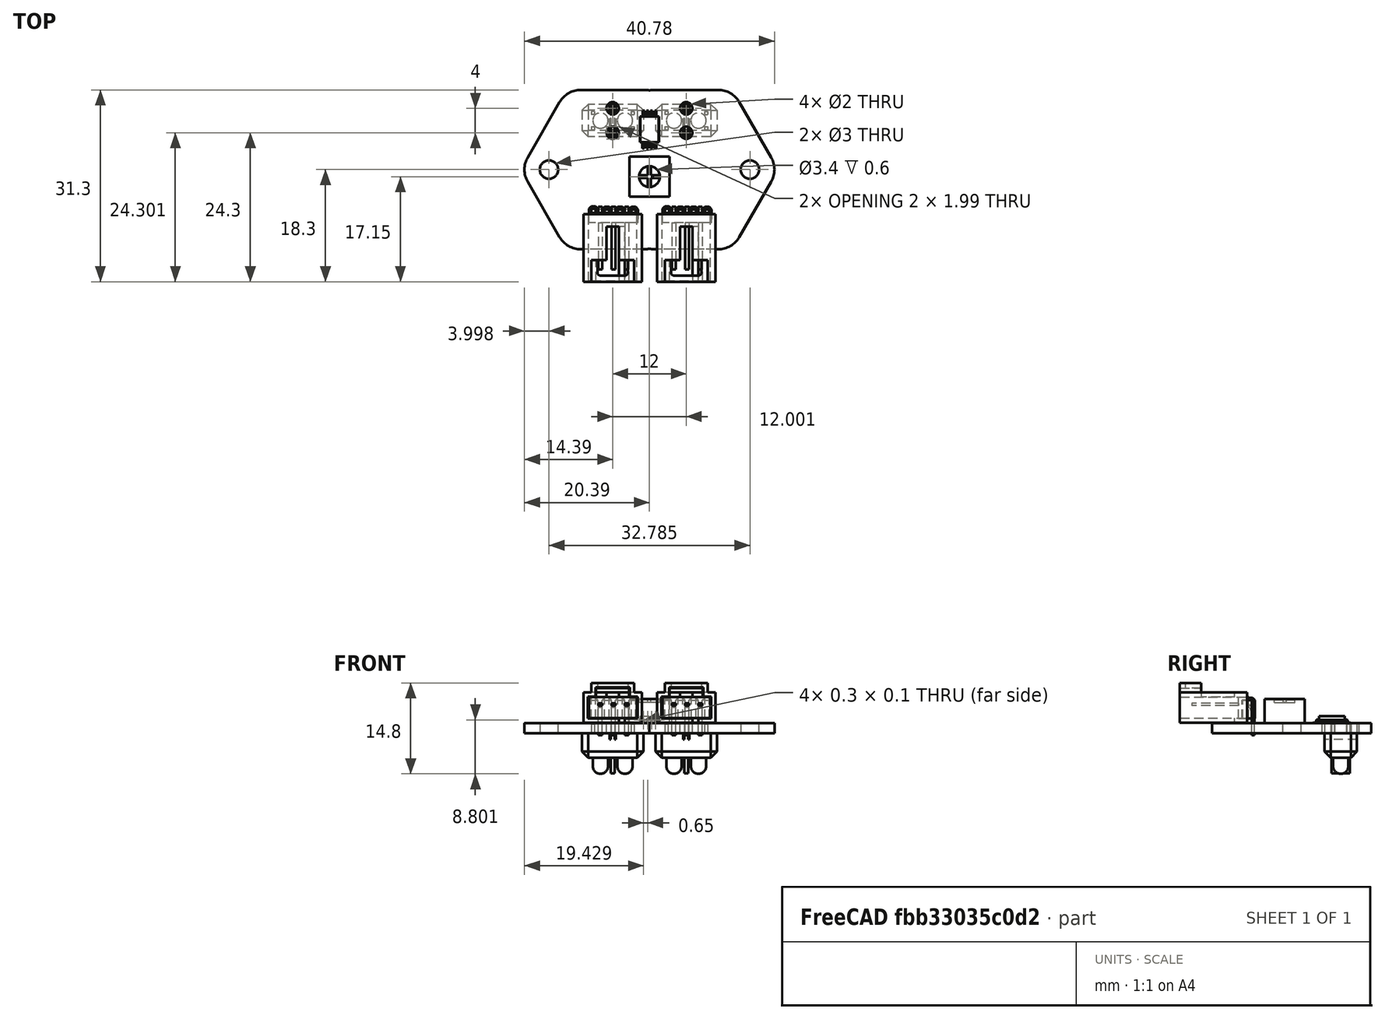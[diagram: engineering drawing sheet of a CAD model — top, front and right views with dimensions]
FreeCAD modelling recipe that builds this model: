
FCSTD DOCUMENT  (FreeCAD 0.14R3692 (Git))
Label: ZumIR_dos
License: CC-BY 3.0
LicenseURL: http://creativecommons.org/licenses/by/3.0/
objects: Part::MultiFuse×7, Part::Cut×6, Part::Cylinder×2, App::DocumentObjectGroup×2
note: 15 computed .brp shape members not serialized (recipe doc carries the construction recipe); baked Part::Feature solids carry a one-line shape summary decoded from their .brp

FEATURE [Part::Cut] Cut  label="Placa_ZumSingle"
FEATURE [Part::Cut] Cut001  label="Placa_ZumSingle001"
  Placement = pos=(12,0,0) rot=(0,0,1;0rad)
FEATURE [Part::MultiFuse] Fusion
  Shapes = -> [Cut,Cut001]
FEATURE [Part::Cylinder] Cylinder  label="Cilindro001"
  Angle = 360
  Height = 10
  Placement = pos=(0,6,-2) rot=(0,0,1;0rad)
  Radius = 1
FEATURE [Part::Cylinder] Cylinder001  label="Cilindro002"
  Angle = 360
  Height = 10
  Placement = pos=(12,6,-2) rot=(0,0,1;0rad)
  Radius = 1
FEATURE [Part::Cut] Cut002
  Base = -> Fusion
  Tool = -> Cylinder
FEATURE [Part::Cut] Cut003
  Base = -> Cut002
  Placement = pos=(-6,0,0) rot=(0,0,1;0rad)
  Tool = -> Cylinder001
FEATURE [Part::MultiFuse] Fusion001  label="Potenciometro001"
  Placement = pos=(0,-1.15,1.6) rot=(0,0,1;0rad)
  Shapes = -> [Cut002,Cut001]
FEATURE [Part::MultiFuse] Fusion002  label="Conectores"
  Placement = pos=(-6,0.7,0.7) rot=(0,0,1;1.5708rad)
FEATURE [Part::Cut] Cut004  label="AlojaConectores"
  Placement = pos=(-6,0.7,0.7) rot=(0,0,1;1.5708rad)
FEATURE [App::DocumentObjectGroup] Grupo  label="GR_Conector"
  Group = -> [Cut004,Fusion002]
FEATURE [Part::MultiFuse] Fusion003  label="Conectores2"
  Placement = pos=(6,0.7,0.7) rot=(0,0,1;1.5708rad)
FEATURE [Part::Cut] Cut005  label="AlojaConectores2"
  Placement = pos=(6,0.7,0.7) rot=(0,0,1;1.5708rad)
FEATURE [App::DocumentObjectGroup] Grupo001  label="GR_Conector2"
  Group = -> [Cut005,Fusion003]
FEATURE [Part::MultiFuse] Fusion004  label="L358"
  Placement = pos=(0,7.2,2.2) rot=(0,0,1;0rad)
FEATURE [Part::MultiFuse] Fusion005  label="ComponentIR"
  Placement = pos=(-6,8,0) rot=(0.707107,-0.707107,0;3.14159rad)
FEATURE [Part::MultiFuse] Fusion006  label="ComponentIR001"
  Placement = pos=(6,8,0) rot=(0.707107,-0.707107,0;3.14159rad)
